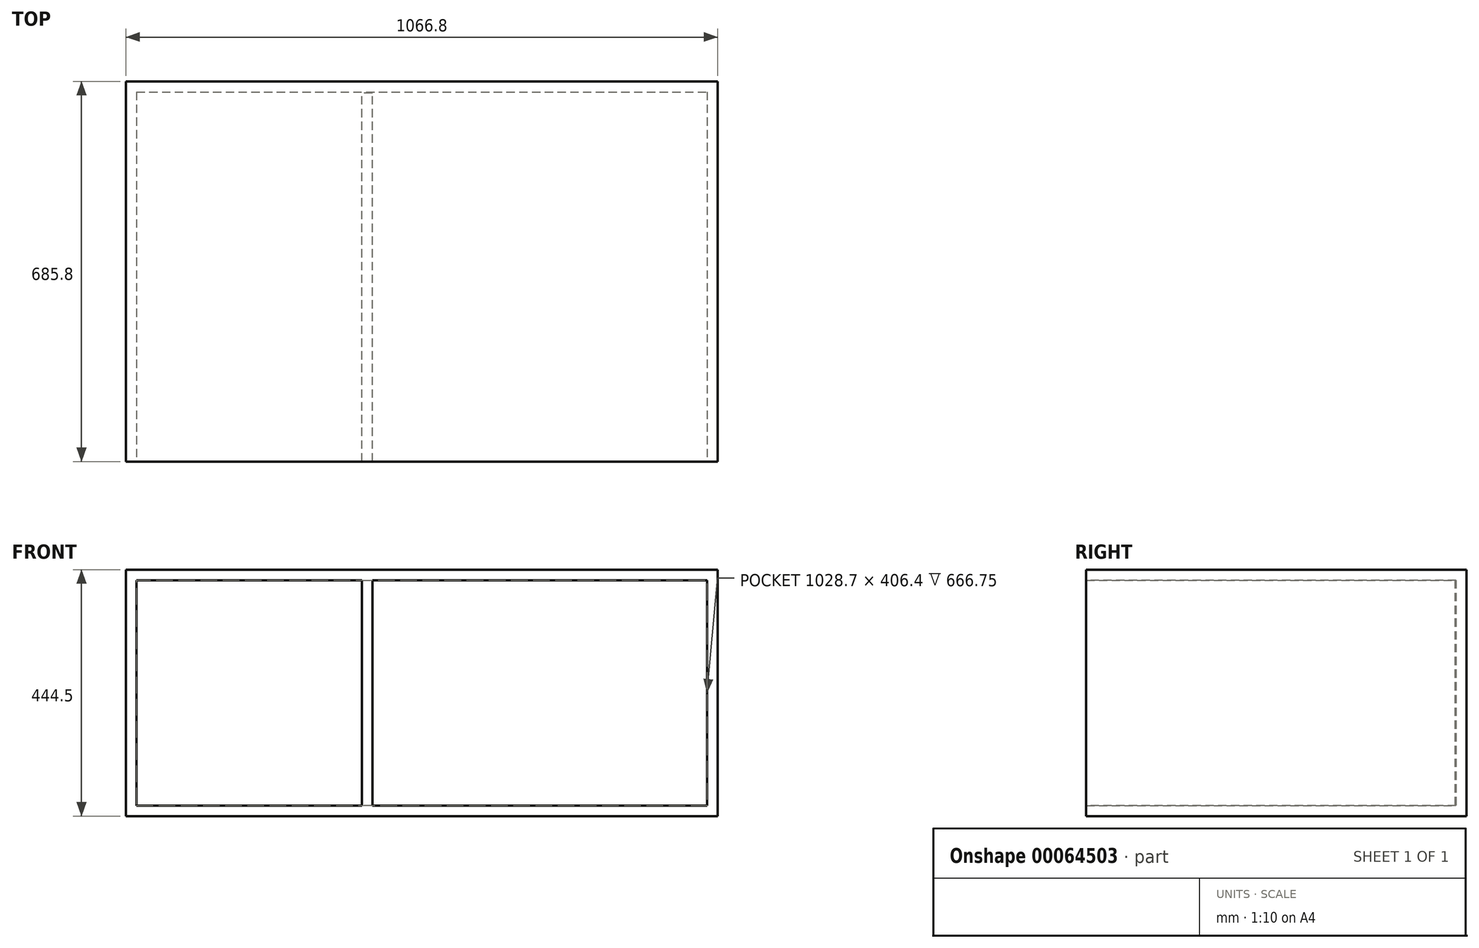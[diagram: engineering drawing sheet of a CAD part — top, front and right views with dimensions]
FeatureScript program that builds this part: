
annotation { "Feature Type Name" : "Feature", "Feature Type Description" : "" }
export const myFeature = defineFeature(function(context is Context, id is Id, definition is map)
    precondition{}
    {
        {
            var Q0;
            Q0=qCreatedBy(makeId("Top.planeOp"),FACE);
            var sketch = newSketch(context, id + "F0", { "sketchPlane" : qUnion([Q0])});
            skLineSegment(sketch, "E0.rect.bottom", {"start": v(533.4, 342.9) * mm, "end": v(-533.4, 342.9) * mm});
            skLineSegment(sketch, "E0.rect.top", {"start": v(533.4, -342.9) * mm, "end": v(-533.4, -342.9) * mm});
            skLineSegment(sketch, "E0.rect.left", {"start": v(533.4, 342.9) * mm, "end": v(533.4, -342.9) * mm});
            skLineSegment(sketch, "E0.rect.right", {"start": v(-533.4, 342.9) * mm, "end": v(-533.4, -342.9) * mm});
            skPoint(sketch, "E0.rect.middle", {"position": v(0, 0) * mm});
            skSolve(sketch);
        }
        {
            var Q0;
            Q0=makeQuery(id+"F0.imprint","IMPRINT",FACE,{"disambiguationData":[TD([[makeQuery(id+"F0.imprint","IMPRINT",EDGE,{"derivedFrom":sQuery(id+"F0.wireOp",EDGE,"E0.rect.bottom")}),1.0]])]});
            extrude(context, id + "F1", {"entities" : qUnion([Q0]), "depth" : 19.05 * mm});
        }
        {
            var Q0;
            Q0=makeQuery(id+"F1.opExtrude","CAP_FACE",FACE,{"disambiguationData":[OSD([sQuery(id+"F0.wireOp",EDGE,"E0.rect.bottom"),sQuery(id+"F0.wireOp",EDGE,"E0.rect.top"),sQuery(id+"F0.wireOp",EDGE,"E0.rect.left"),sQuery(id+"F0.wireOp",EDGE,"E0.rect.right")])],"isStart":false});
            var sketch = newSketch(context, id + "F2", { "sketchPlane" : qUnion([Q0])});
            skLineSegment(sketch, "E1.rect.bottom", {"start": v(-514.35, 323.85) * mm, "end": v(-533.4, 323.85) * mm});
            skLineSegment(sketch, "E1.rect.top", {"start": v(-514.35, -342.9) * mm, "end": v(-533.4, -342.9) * mm});
            skLineSegment(sketch, "E1.rect.left", {"start": v(-514.35, 323.85) * mm, "end": v(-514.35, -342.9) * mm});
            skLineSegment(sketch, "E1.rect.right", {"start": v(-533.4, 323.85) * mm, "end": v(-533.4, -342.9) * mm});
            skPoint(sketch, "E1.rect.middle", {"position": v(-523.88, -9.52) * mm});
            skLineSegment(sketch, "E2", {"start": v(0, -342.9) * mm, "end": v(0, 342.9) * mm, "construction": true});
            skLineSegment(sketch, "E3.MirrorCS", {"start": v(514.35, -342.9) * mm, "end": v(533.4, -342.9) * mm});
            skLineSegment(sketch, "E4.MirrorCS", {"start": v(514.35, 323.85) * mm, "end": v(533.4, 323.85) * mm});
            skLineSegment(sketch, "E5.MirrorCS", {"start": v(514.35, 323.85) * mm, "end": v(514.35, -342.9) * mm});
            skLineSegment(sketch, "E6.MirrorCS", {"start": v(533.4, 323.85) * mm, "end": v(533.4, -342.9) * mm});
            skPoint(sketch, "E7.MirrorP", {"position": v(523.88, -9.52) * mm});
            skLineSegment(sketch, "E8.bottom", {"start": v(-88.9, -342.9) * mm, "end": v(-107.95, -342.9) * mm});
            skLineSegment(sketch, "E8.top", {"start": v(-88.9, 321.73) * mm, "end": v(-107.95, 321.73) * mm});
            skLineSegment(sketch, "E8.left", {"start": v(-88.9, -342.9) * mm, "end": v(-88.9, 321.73) * mm});
            skLineSegment(sketch, "E8.right", {"start": v(-107.95, -342.9) * mm, "end": v(-107.95, 321.73) * mm});
            skLineSegment(sketch, "E9.bottom", {"start": v(-533.4, 342.9) * mm, "end": v(533.4, 342.9) * mm});
            skLineSegment(sketch, "E9.top", {"start": v(-533.4, 323.85) * mm, "end": v(533.4, 323.85) * mm});
            skLineSegment(sketch, "E9.left", {"start": v(-533.4, 342.9) * mm, "end": v(-533.4, 323.85) * mm});
            skLineSegment(sketch, "E9.right", {"start": v(533.4, 342.9) * mm, "end": v(533.4, 323.85) * mm});
            skSolve(sketch);
        }
        {
            var Q0;
            Q0 = qSketchRegion(id + "F2", true);
            extrude(context, id + "F3", {"entities" : qUnion([Q0]), "operationType" : NewBodyOperationType.ADD, "depth" : 406.4 * mm});
        }
        {
            var Q0;
            Q0=makeQuery(id+"F1.opExtrude","CAP_FACE",FACE,{"disambiguationData":[OSD([sQuery(id+"F0.wireOp",EDGE,"E0.rect.bottom"),sQuery(id+"F0.wireOp",EDGE,"E0.rect.top"),sQuery(id+"F0.wireOp",EDGE,"E0.rect.left"),sQuery(id+"F0.wireOp",EDGE,"E0.rect.right")])],"isStart":false});
            cPlane(context, id + "F4", {"entities" : qUnion([Q0]), "cplaneType" : CPlaneType.OFFSET, "offset" : 406.4 * mm, "width" : 152.4 * mm, "height" : 152.4 * mm});
        }
        {
            var Q0;
            Q0=qCreatedBy(id+"F4.planeOp",FACE);
            var sketch = newSketch(context, id + "F5", { "sketchPlane" : qUnion([Q0])});
            skLineSegment(sketch, "E10.rect.bottom", {"start": v(-533.4, 342.9) * mm, "end": v(533.4, 342.9) * mm});
            skLineSegment(sketch, "E10.rect.top", {"start": v(-533.4, -342.9) * mm, "end": v(533.4, -342.9) * mm});
            skLineSegment(sketch, "E10.rect.left", {"start": v(-533.4, 342.9) * mm, "end": v(-533.4, -342.9) * mm});
            skLineSegment(sketch, "E10.rect.right", {"start": v(533.4, 342.9) * mm, "end": v(533.4, -342.9) * mm});
            skPoint(sketch, "E10.rect.middle", {"position": v(0, 0) * mm});
            skSolve(sketch);
        }
        {
            var Q0;
            Q0=makeQuery(id+"F5.imprint","IMPRINT",FACE,{"disambiguationData":[TD([[makeQuery(id+"F5.imprint","IMPRINT",EDGE,{"derivedFrom":sQuery(id+"F5.wireOp",EDGE,"E10.rect.bottom")}),-1.0]])]});
            extrude(context, id + "F6", {"entities" : qUnion([Q0]), "operationType" : NewBodyOperationType.ADD, "depth" : 19.05 * mm});
        }
    });
